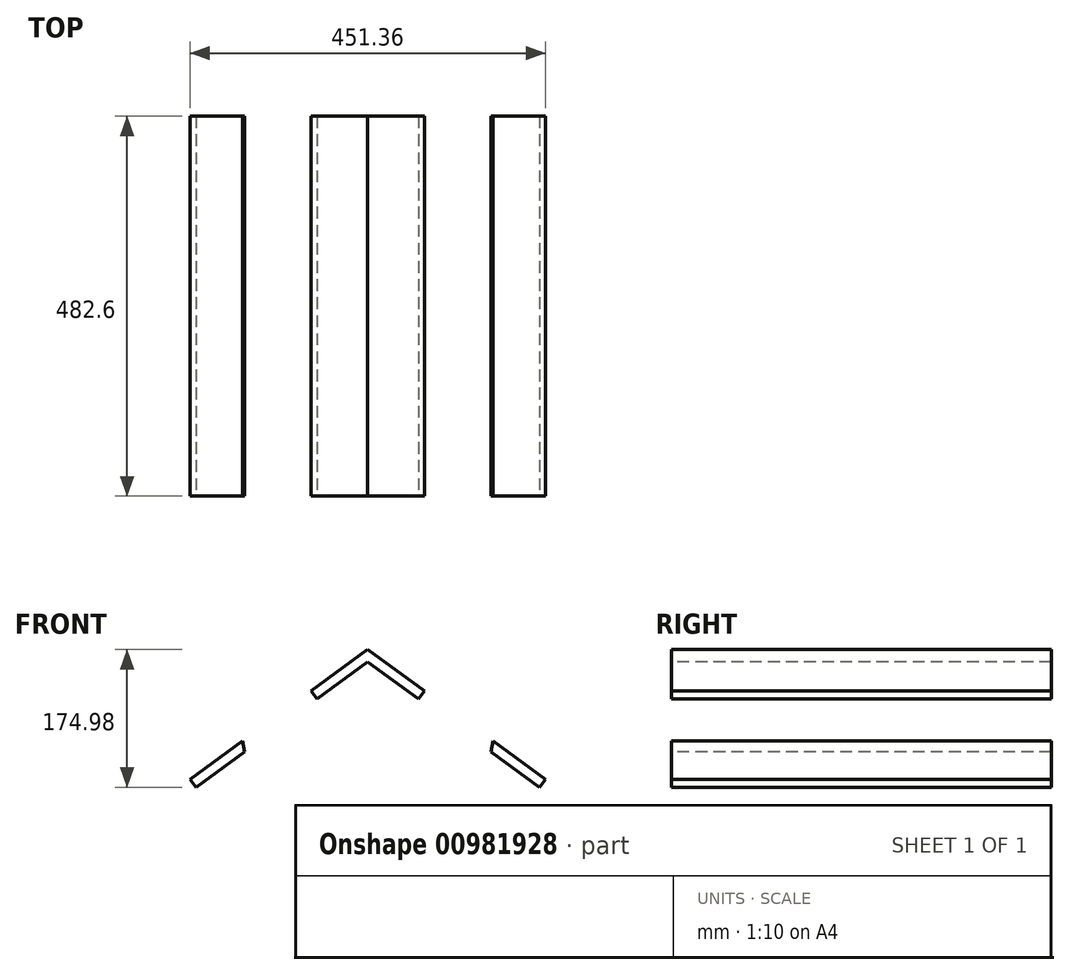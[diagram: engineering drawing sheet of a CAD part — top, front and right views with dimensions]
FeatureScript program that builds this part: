
annotation { "Feature Type Name" : "Feature", "Feature Type Description" : "" }
export const myFeature = defineFeature(function(context is Context, id is Id, definition is map)
    precondition{}
    {
        {
            var Q0;
            Q0=qCreatedBy(makeId("Front.planeOp"),FACE);
            var sketch = newSketch(context, id + "F0", { "sketchPlane" : qUnion([Q0])});
            skLineSegment(sketch, "E0.bottom", {"start": v(0, 0) * mm, "end": v(-161.93, 0) * mm});
            skLineSegment(sketch, "E0.top", {"start": v(0, 134.94) * mm, "end": v(-161.93, 134.94) * mm});
            skLineSegment(sketch, "E0.left", {"start": v(0, 0) * mm, "end": v(0, 134.94) * mm});
            skLineSegment(sketch, "E0.right", {"start": v(-161.93, 0) * mm, "end": v(-161.92, 134.94) * mm});
            skArc(sketch, "E1", {"start": v(0, 134.94) * mm, "mid": v(-80.96, 215.9) * mm, "end": v(-161.92, 134.94) * mm});
            skLineSegment(sketch, "E2", {"start": v(-195.26, -19.05) * mm, "end": v(33.34, -19.05) * mm});
            skLineSegment(sketch, "E3", {"start": v(33.34, -19.05) * mm, "end": v(78.18, 198.23) * mm});
            skLineSegment(sketch, "E4", {"start": v(78.18, 198.23) * mm, "end": v(-80.96, 314.38) * mm});
            skLineSegment(sketch, "E5", {"start": v(-80.96, 314.38) * mm, "end": v(-240.1, 198.23) * mm});
            skLineSegment(sketch, "E6", {"start": v(-240.1, 198.23) * mm, "end": v(-195.26, -19.05) * mm});
            skLineSegment(sketch, "E7", {"start": v(-80.96, 314.38) * mm, "end": v(-306.64, 149.66) * mm});
            skLineSegment(sketch, "E8", {"start": v(-80.96, 314.38) * mm, "end": v(144.72, 149.66) * mm});
            skLineSegment(sketch, "E9", {"start": v(-306.64, 149.66) * mm, "end": v(-299.15, 139.4) * mm});
            skLineSegment(sketch, "E10", {"start": v(-299.15, 139.4) * mm, "end": v(-80.96, 298.66) * mm});
            skLineSegment(sketch, "E11", {"start": v(-80.96, 298.66) * mm, "end": v(-80.96, 314.38) * mm});
            skLineSegment(sketch, "E12.MirrorCS", {"start": v(137.23, 139.4) * mm, "end": v(-80.96, 298.66) * mm});
            skLineSegment(sketch, "E13.MirrorCS", {"start": v(144.72, 149.66) * mm, "end": v(137.23, 139.4) * mm});
            skLineSegment(sketch, "E14", {"start": v(-199.2, 0) * mm, "end": v(-161.93, 0) * mm});
            skLineSegment(sketch, "E15", {"start": v(0, 0) * mm, "end": v(37.27, 0) * mm});
            skLineSegment(sketch, "E16", {"start": v(-226.01, 192.79) * mm, "end": v(-186.23, 0) * mm});
            skLineSegment(sketch, "E17.MirrorCS", {"start": v(64.09, 192.79) * mm, "end": v(24.3, 0) * mm});
            skLineSegment(sketch, "E18", {"start": v(-237.28, 184.56) * mm, "end": v(-226.01, 192.79) * mm});
            skLineSegment(sketch, "E19", {"start": v(64.09, 192.79) * mm, "end": v(75.36, 184.56) * mm});
            skPoint(sketch, "E20", {"position": v(-80.96, -19.05) * mm});
            skLineSegment(sketch, "E21", {"start": v(-196.57, -12.7) * mm, "end": v(34.65, -12.7) * mm});
            skLineSegment(sketch, "E22", {"start": v(-152.77, 261.97) * mm, "end": v(-145.28, 251.71) * mm});
            skLineSegment(sketch, "E23.MirrorCS", {"start": v(-9.16, 261.97) * mm, "end": v(-16.64, 251.71) * mm});
            skLineSegment(sketch, "E24", {"start": v(-80.96, -12.7) * mm, "end": v(-80.96, 0) * mm});
            skLineSegment(sketch, "E25", {"start": v(-235.89, 177.8) * mm, "end": v(61, 177.8) * mm});
            skLineSegment(sketch, "E26", {"start": v(-106.78, 317.5) * mm, "end": v(-55.15, 317.5) * mm});
            skLineSegment(sketch, "E27", {"start": v(73.96, 177.8) * mm, "end": v(61, 177.8) * mm});
            skSolve(sketch);
        }
        {
            var Q0;
            {var subQ5=sQuery(id+"F0.wireOp",EDGE,"E9");Q0=makeQuery(id+"F0.imprint","IMPRINT",FACE,{"disambiguationData":[TD([[makeQuery(id+"F0.imprint","IMPRINT",EDGE,{"derivedFrom":subQ5}),1.0]])]});}
            var Q1;
            {var subQ1=sQuery(id+"F0.wireOp",EDGE,"E11");Q1=makeQuery(id+"F0.imprint","IMPRINT",FACE,{"disambiguationData":[TD([[makeQuery(id+"F0.imprint","IMPRINT",EDGE,{"derivedFrom":subQ1}),-1.0]])]});}
            var Q2;
            {var subQ0=sQuery(id+"F0.wireOp",EDGE,"E11");Q2=makeQuery(id+"F0.imprint","IMPRINT",FACE,{"disambiguationData":[TD([[makeQuery(id+"F0.imprint","IMPRINT",EDGE,{"derivedFrom":subQ0}),1.0]])]});}
            var Q3;
            {var subQ5=sQuery(id+"F0.wireOp",EDGE,"E13.MirrorCS");Q3=makeQuery(id+"F0.imprint","IMPRINT",FACE,{"disambiguationData":[TD([[makeQuery(id+"F0.imprint","IMPRINT",EDGE,{"derivedFrom":subQ5}),-1.0]])]});}
            extrude(context, id + "F1", {"entities" : qUnion([Q0, Q1, Q2, Q3]), "oppositeDirection" : true, "depth" : 457.2 * mm, "offsetDistance" : 25.4 * mm, "hasSecondDirection" : true, "secondDirectionOppositeDirection" : false, "secondDirectionDepth" : 25.4 * mm});
        }
    });
